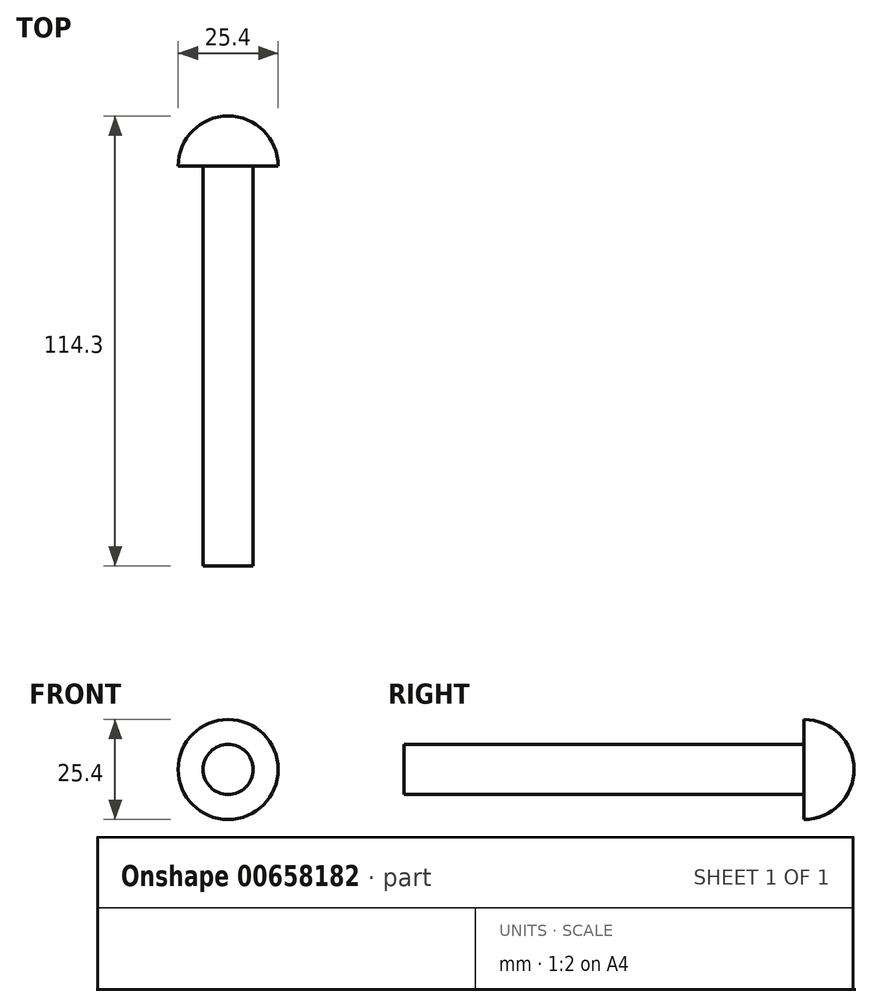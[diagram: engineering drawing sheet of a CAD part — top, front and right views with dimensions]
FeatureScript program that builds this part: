
annotation { "Feature Type Name" : "Feature", "Feature Type Description" : "" }
export const myFeature = defineFeature(function(context is Context, id is Id, definition is map)
    precondition{}
    {
        {
            var Q0;
            Q0=qCreatedBy(makeId("Front.planeOp"),FACE);
            var sketch = newSketch(context, id + "F0", { "sketchPlane" : qUnion([Q0])});
            skCircle(sketch, "E0", {"center": v(0, 0) * mm, "radius": 6.35 * mm});
            skSolve(sketch);
        }
        {
            var Q0;
            Q0 = qSketchRegion(id + "F0", true);
            extrude(context, id + "F1", {"entities" : qUnion([Q0]), "depth" : 101.6 * mm, "offsetDistance" : 25.4 * mm});
        }
        {
            var Q0;
            Q0=qCreatedBy(makeId("Right.planeOp"),FACE);
            var sketch = newSketch(context, id + "F2", { "sketchPlane" : qUnion([Q0])});
            skLineSegment(sketch, "E1", {"start": v(0, 0) * mm, "end": v(12.7, 0) * mm});
            skLineSegment(sketch, "E2", {"start": v(12.7, 0) * mm, "end": v(0, 0) * mm});
            skLineSegment(sketch, "E3", {"start": v(0, 0) * mm, "end": v(0, 12.7) * mm});
            skArc(sketch, "E4", {"start": v(0, 12.7) * mm, "mid": v(8.98, 8.98) * mm, "end": v(12.7, 0) * mm});
            skSolve(sketch);
        }
        {
            var Q0;
            Q0 = qSketchRegion(id + "F2", true);
            var Q1;
            Q1=sQuery(id+"F2.wireOp",EDGE,"E2");
            revolve(context, id + "F3", {"operationType" : NewBodyOperationType.ADD, "entities" : qUnion([Q0]), "axis" : qUnion([Q1]), "revolveType" : RevolveType.FULL});
        }
    });
